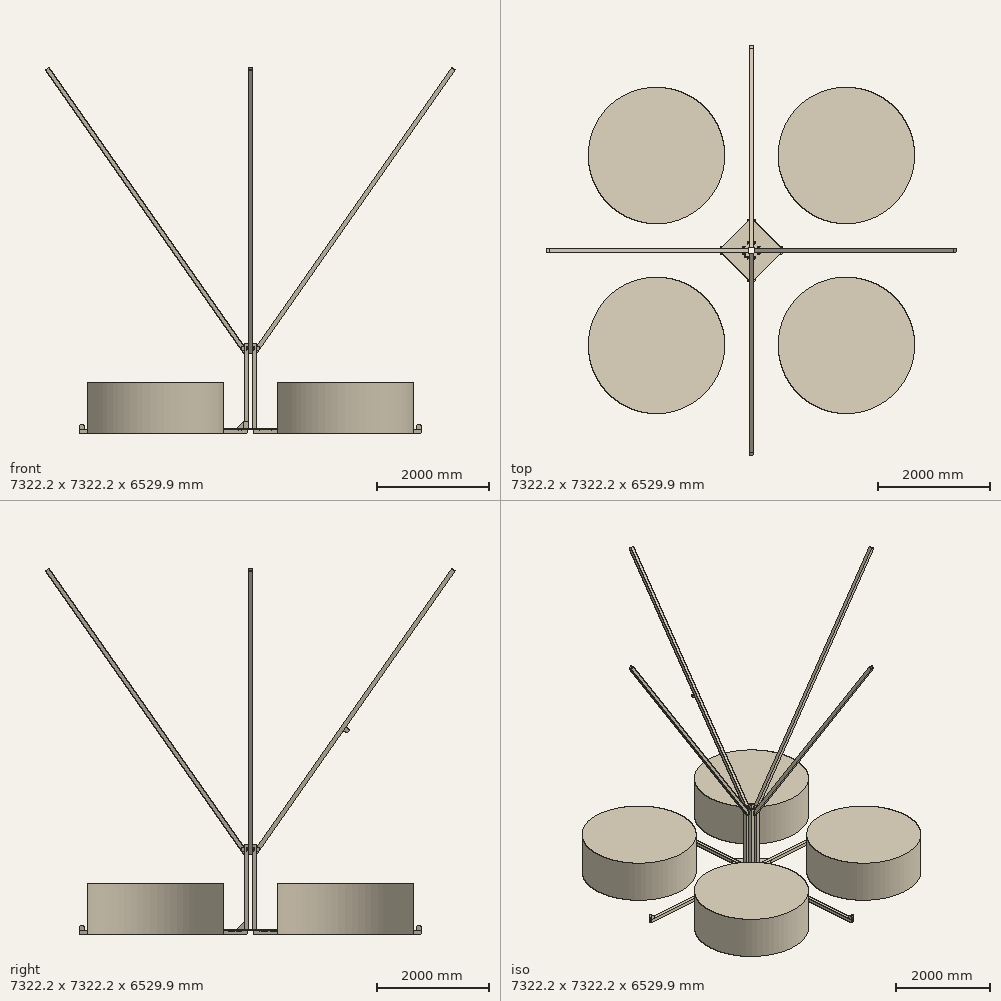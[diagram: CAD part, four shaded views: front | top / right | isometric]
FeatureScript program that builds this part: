
annotation { "Feature Type Name" : "Feature", "Feature Type Description" : "" }
export const myFeature = defineFeature(function(context is Context, id is Id, definition is map)
    precondition{}
    {
        {
            var Q0;
            Q0=qCreatedBy(makeId("Right.planeOp"),FACE);
            cPlane(context, id + "F0", {"entities" : qUnion([Q0]), "cplaneType" : CPlaneType.OFFSET, "offset" : 50.8 * mm, "oppositeDirection" : true, "width" : 152.4 * mm, "height" : 152.4 * mm});
        }
        {
            var Q0;
            Q0=qCreatedBy(id+"F0.planeOp",FACE);
            var sketch = newSketch(context, id + "F1", { "sketchPlane" : qUnion([Q0])});
            skLineSegment(sketch, "E0.bottom", {"start": v(38.1, 38.1) * mm, "end": v(-38.1, 38.1) * mm});
            skLineSegment(sketch, "E0.top", {"start": v(38.1, -38.1) * mm, "end": v(-38.1, -38.1) * mm});
            skLineSegment(sketch, "E0.left", {"start": v(38.1, 38.1) * mm, "end": v(38.1, -38.1) * mm});
            skLineSegment(sketch, "E0.right", {"start": v(-38.1, 38.1) * mm, "end": v(-38.1, -38.1) * mm});
            skPoint(sketch, "E0.middle", {"position": v(0, 0) * mm});
            skLineSegment(sketch, "E1.bottom", {"start": v(35.43, 35.43) * mm, "end": v(-35.43, 35.43) * mm});
            skLineSegment(sketch, "E1.top", {"start": v(35.43, -35.43) * mm, "end": v(-35.43, -35.43) * mm});
            skLineSegment(sketch, "E1.left", {"start": v(35.43, 35.43) * mm, "end": v(35.43, -35.43) * mm});
            skLineSegment(sketch, "E1.right", {"start": v(-35.43, 35.43) * mm, "end": v(-35.43, -35.43) * mm});
            skSolve(sketch);
        }
        {
            var Q0;
            Q0=makeQuery(id+"F1.imprint","IMPRINT",FACE,{"disambiguationData":[TD([[makeQuery(id+"F1.imprint","IMPRINT",EDGE,{"derivedFrom":sQuery(id+"F1.wireOp",EDGE,"E0.bottom")}),1.0]])]});
            extrude(context, id + "F2", {"entities" : qUnion([Q0]), "oppositeDirection" : true, "depth" : 2997.2 * mm});
        }
        {
            var Q0;
            Q0=qCreatedBy(makeId("Right.planeOp"),FACE);
            var sketch = newSketch(context, id + "F3", { "sketchPlane" : qUnion([Q0])});
            skLineSegment(sketch, "E2", {"start": v(0, 0) * mm, "end": v(0, 32.07) * mm, "construction": true});
            skSolve(sketch);
        }
        {
            var Q0;
            Q0=makeQuery(id+"F2.opExtrude","SWEPT_BODY",BODY,{"disambiguationData":[OSD([sQuery(id+"F1.wireOp",EDGE,"E0.bottom"),sQuery(id+"F1.wireOp",EDGE,"E0.top"),sQuery(id+"F1.wireOp",EDGE,"E0.left"),sQuery(id+"F1.wireOp",EDGE,"E0.right"),sQuery(id+"F1.wireOp",EDGE,"E1.bottom"),sQuery(id+"F1.wireOp",EDGE,"E1.top"),sQuery(id+"F1.wireOp",EDGE,"E1.left"),sQuery(id+"F1.wireOp",EDGE,"E1.right")])]});
            var Q1;
            Q1=sQuery(id+"F3.wireOp",EDGE,"E2");
            circularPattern(context, id + "F4", {"entities" : qUnion([Q0]), "axis" : qUnion([Q1]), "angle" : 90 * degree, "instanceCount" : 4});
        }
        {
            var Q0;
            Q0=qCreatedBy(id+"F0.planeOp",FACE);
            cPlane(context, id + "F5", {"entities" : qUnion([Q0]), "cplaneType" : CPlaneType.OFFSET, "offset" : 88.9 * mm, "oppositeDirection" : true, "width" : 152.4 * mm, "height" : 152.4 * mm});
        }
        {
            var Q0;
            Q0=qCreatedBy(id+"F5.planeOp",FACE);
            var sketch = newSketch(context, id + "F6", { "sketchPlane" : qUnion([Q0])});
            skLineSegment(sketch, "E3", {"start": v(-38.1, 38.1) * mm, "end": v(-63.5, 38.1) * mm});
            skLineSegment(sketch, "E4", {"start": v(-63.5, 38.1) * mm, "end": v(-63.5, 34.93) * mm});
            skLineSegment(sketch, "E5", {"start": v(-63.5, 34.93) * mm, "end": v(-28.58, 34.93) * mm});
            skLineSegment(sketch, "E6", {"start": v(-28.58, 34.93) * mm, "end": v(-28.57, 12.7) * mm});
            skLineSegment(sketch, "E7", {"start": v(-38.1, 12.7) * mm, "end": v(-28.57, 12.7) * mm});
            skLineSegment(sketch, "E8", {"start": v(-38.1, 12.7) * mm, "end": v(-38.1, 38.1) * mm});
            skSolve(sketch);
        }
        {
            var Q0;
            Q0 = qSketchRegion(id + "F6", true);
            extrude(context, id + "F7", {"entities" : qUnion([Q0]), "oppositeDirection" : true, "depth" : 406.4 * mm});
        }
        {
            var Q0;
            Q0=makeQuery(id+"F7.opExtrude","SWEPT_BODY",BODY,{"disambiguationData":[OSD([sQuery(id+"F6.wireOp",EDGE,"E3"),sQuery(id+"F6.wireOp",EDGE,"E4"),sQuery(id+"F6.wireOp",EDGE,"E5"),sQuery(id+"F6.wireOp",EDGE,"E6"),sQuery(id+"F6.wireOp",EDGE,"E7"),sQuery(id+"F6.wireOp",EDGE,"E8")])]});
            var Q1;
            Q1=qCreatedBy(makeId("Front.planeOp"),FACE);
            mirror(context, id + "F8", {"entities" : qUnion([Q0]), "mirrorPlane" : qUnion([Q1])});
        }
        {
            var Q0;
            Q0=makeQuery(id+"F7.opExtrude","SWEPT_BODY",BODY,{"disambiguationData":[OSD([sQuery(id+"F6.wireOp",EDGE,"E3"),sQuery(id+"F6.wireOp",EDGE,"E4"),sQuery(id+"F6.wireOp",EDGE,"E5"),sQuery(id+"F6.wireOp",EDGE,"E6"),sQuery(id+"F6.wireOp",EDGE,"E7"),sQuery(id+"F6.wireOp",EDGE,"E8")])]});
            var Q1;
            Q1=makeQuery(id+"F8.opPattern","COPY",BODY,{"derivedFrom":makeQuery(id+"F7.opExtrude","SWEPT_BODY",BODY,{"disambiguationData":[OSD([sQuery(id+"F6.wireOp",EDGE,"E3"),sQuery(id+"F6.wireOp",EDGE,"E4"),sQuery(id+"F6.wireOp",EDGE,"E5"),sQuery(id+"F6.wireOp",EDGE,"E6"),sQuery(id+"F6.wireOp",EDGE,"E7"),sQuery(id+"F6.wireOp",EDGE,"E8")])]}),"instanceName":"1"});
            var Q2;
            Q2=sQuery(id+"F3.wireOp",EDGE,"E2");
            circularPattern(context, id + "F9", {"entities" : qUnion([Q0, Q1]), "axis" : qUnion([Q2]), "angle" : 90 * degree, "instanceCount" : 4});
        }
        {
            var Q0;
            Q0=qCreatedBy(makeId("Right.planeOp"),FACE);
            var sketch = newSketch(context, id + "F10", { "sketchPlane" : qUnion([Q0])});
            skLineSegment(sketch, "E9", {"start": v(0, 0) * mm, "end": v(0, 43.8) * mm});
            skSolve(sketch);
        }
        {
            var Q0;
            Q0=makeQuery(id+"F7.opExtrude","SWEPT_FACE",FACE,{"disambiguationData":[OSD([sQuery(id+"F6.wireOp",EDGE,"E3")])]});
            var sketch = newSketch(context, id + "F11", { "sketchPlane" : qUnion([Q0])});
            skLineSegment(sketch, "E10.0", {"start": v(-546.1, -38.1) * mm, "end": v(-139.7, -38.1) * mm, "construction": true});
            skLineSegment(sketch, "E10.1", {"start": v(-38.1, -3048) * mm, "end": v(-38.1, -50.8) * mm, "construction": true});
            skLineSegment(sketch, "E10.3", {"start": v(-38.1, -546.1) * mm, "end": v(-63.5, -546.1) * mm, "construction": true});
            skLineSegment(sketch, "E11", {"start": v(-546.1, -38.1) * mm, "end": v(-38.1, -546.1) * mm});
            skLineSegment(sketch, "E12", {"start": v(-38.1, -63.5) * mm, "end": v(-63.5, -38.1) * mm});
            skLineSegment(sketch, "E13", {"start": v(-63.5, -38.1) * mm, "end": v(-546.1, -38.1) * mm});
            skLineSegment(sketch, "E14", {"start": v(-546.1, -38.1) * mm, "end": v(-63.5, -38.1) * mm});
            skLineSegment(sketch, "E15", {"start": v(-38.1, -546.1) * mm, "end": v(-38.1, -63.5) * mm});
            skLineSegment(sketch, "E16", {"start": v(-50.8, -50.8) * mm, "end": v(-292.1, -292.1) * mm, "construction": true});
            skLineSegment(sketch, "E17", {"start": v(-171.45, -171.45) * mm, "end": v(-225.33, -225.33) * mm});
            skLineSegment(sketch, "E18", {"start": v(-225.33, -225.33) * mm, "end": v(-494.74, 44.08) * mm, "construction": true});
            skLineSegment(sketch, "E19", {"start": v(-494.74, 44.08) * mm, "end": v(-386.98, 151.84) * mm, "construction": true});
            skLineSegment(sketch, "E20", {"start": v(-386.98, 151.84) * mm, "end": v(-117.57, -117.57) * mm, "construction": true});
            skLineSegment(sketch, "E21", {"start": v(-117.57, -117.57) * mm, "end": v(-171.45, -171.45) * mm});
            skSolve(sketch);
        }
        {
            var Q0;
            Q0 = qSketchRegion(id + "F11", true);
            extrude(context, id + "F12", {"entities" : qUnion([Q0]), "depth" : 3.17 * mm});
        }
        {
            var Q0;
            Q0=makeQuery(id+"F12.opExtrude","SWEPT_BODY",BODY,{"disambiguationData":[OSD([sQuery(id+"F11.wireOp",EDGE,"E11"),sQuery(id+"F11.wireOp",EDGE,"E12"),sQuery(id+"F11.wireOp",EDGE,"E14"),sQuery(id+"F11.wireOp",EDGE,"E15")])]});
            var Q1;
            Q1=sQuery(id+"F10.wireOp",EDGE,"E9");
            circularPattern(context, id + "F13", {"entities" : qUnion([Q0]), "axis" : qUnion([Q1]), "angle" : 90 * degree, "instanceCount" : 4});
        }
        {
            var Q0;
            Q0=makeQuery(id+"F2.opExtrude","SWEPT_FACE",FACE,{"disambiguationData":[OSD([sQuery(id+"F1.wireOp",EDGE,"E0.bottom")])]});
            var sketch = newSketch(context, id + "F14", { "sketchPlane" : qUnion([Q0])});
            skLineSegment(sketch, "E22.bottom", {"start": v(-3048, 38.1) * mm, "end": v(-2971.8, 38.1) * mm});
            skLineSegment(sketch, "E22.top", {"start": v(-3048, -38.1) * mm, "end": v(-2971.8, -38.1) * mm});
            skLineSegment(sketch, "E22.left", {"start": v(-3048, 38.1) * mm, "end": v(-3048, -38.1) * mm});
            skLineSegment(sketch, "E22.right", {"start": v(-2971.8, 38.1) * mm, "end": v(-2971.8, -38.1) * mm});
            skSolve(sketch);
        }
        {
            var Q0;
            Q0=makeQuery(id+"F14.imprint","IMPRINT",FACE,{"disambiguationData":[TD([[makeQuery(id+"F14.imprint","IMPRINT",EDGE,{"derivedFrom":sQuery(id+"F14.wireOp",EDGE,"E22.bottom")}),-1.0]])]});
            extrude(context, id + "F15", {"entities" : qUnion([Q0]), "depth" : 6.35 * mm});
        }
        {
            var Q0;
            Q0=makeQuery(id+"F15.opExtrude","SWEPT_FACE",FACE,{"disambiguationData":[OSD([sQuery(id+"F14.wireOp",EDGE,"E22.top")])]});
            var sketch = newSketch(context, id + "F16", { "sketchPlane" : qUnion([Q0])});
            skLineSegment(sketch, "E23.bottom", {"start": v(-2971.8, 44.45) * mm, "end": v(-3048, 44.45) * mm});
            skLineSegment(sketch, "E23.top", {"start": v(-2971.8, 82.55) * mm, "end": v(-3048, 82.55) * mm});
            skLineSegment(sketch, "E23.left", {"start": v(-2971.8, 44.45) * mm, "end": v(-2971.8, 82.55) * mm});
            skLineSegment(sketch, "E23.right", {"start": v(-3048, 44.45) * mm, "end": v(-3048, 82.55) * mm});
            skArc(sketch, "E24", {"start": v(-2971.8, 82.55) * mm, "mid": v(-3009.9, 120.65) * mm, "end": v(-3048, 82.55) * mm});
            skCircle(sketch, "E25", {"center": v(-3009.9, 82.55) * mm, "radius": 6.35 * mm});
            skSolve(sketch);
        }
        {
            var Q0;
            {var subQ0=sQuery(id+"F16.wireOp",EDGE,"E24");Q0=makeQuery(id+"F16.imprint","IMPRINT",FACE,{"disambiguationData":[TD([[makeQuery(id+"F16.imprint","IMPRINT",EDGE,{"derivedFrom":subQ0}),1.0]])]});}
            var Q1;
            Q1=makeQuery(id+"F16.imprint","IMPRINT",FACE,{"disambiguationData":[TD([[makeQuery(id+"F16.imprint","IMPRINT",EDGE,{"derivedFrom":sQuery(id+"F16.wireOp",EDGE,"E23.bottom")}),1.0]])]});
            extrude(context, id + "F17", {"entities" : qUnion([Q0, Q1]), "oppositeDirection" : true, "depth" : 6.35 * mm});
        }
        {
            var Q0;
            Q0=makeQuery(id+"F17.opExtrude","SWEPT_BODY",BODY,{"disambiguationData":[OSD([sQuery(id+"F16.wireOp",EDGE,"E23.bottom"),sQuery(id+"F16.wireOp",EDGE,"E23.left"),sQuery(id+"F16.wireOp",EDGE,"E23.right"),sQuery(id+"F16.wireOp",EDGE,"E24"),sQuery(id+"F16.wireOp",EDGE,"E25")])]});
            var Q1;
            Q1=qCreatedBy(makeId("Front.planeOp"),FACE);
            mirror(context, id + "F18", {"operationType" : NewBodyOperationType.ADD, "entities" : qUnion([Q0]), "mirrorPlane" : qUnion([Q1])});
        }
        {
            var Q0;
            Q0=makeQuery(id+"F15.opExtrude","SWEPT_BODY",BODY,{"disambiguationData":[OSD([sQuery(id+"F14.wireOp",EDGE,"E22.bottom"),sQuery(id+"F14.wireOp",EDGE,"E22.top"),sQuery(id+"F14.wireOp",EDGE,"E22.left"),sQuery(id+"F14.wireOp",EDGE,"E22.right")])]});
            var Q1;
            Q1=sQuery(id+"F10.wireOp",EDGE,"E9");
            circularPattern(context, id + "F19", {"entities" : qUnion([Q0]), "axis" : qUnion([Q1]), "angle" : 90 * degree, "instanceCount" : 4});
        }
        {
            var Q0;
            Q0=makeQuery(id+"F13.opPattern","COPY",FACE,{"derivedFrom":makeQuery(id+"F12.opExtrude","CAP_FACE",FACE,{"disambiguationData":[OSD([sQuery(id+"F11.wireOp",EDGE,"E11"),sQuery(id+"F11.wireOp",EDGE,"E12"),sQuery(id+"F11.wireOp",EDGE,"E14"),sQuery(id+"F11.wireOp",EDGE,"E15")])],"isStart":false}),"instanceName":"3"});
            var sketch = newSketch(context, id + "F20", { "sketchPlane" : qUnion([Q0])});
            skLineSegment(sketch, "E26.0", {"start": v(-3048, 38.1) * mm, "end": v(-50.8, 38.1) * mm, "construction": true});
            skLineSegment(sketch, "E26.1", {"start": v(-38.1, 3048) * mm, "end": v(-38.1, 50.8) * mm, "construction": true});
            skLineSegment(sketch, "E27", {"start": v(-50.8, 38.1) * mm, "end": v(-38.1, 38.1) * mm});
            skLineSegment(sketch, "E28", {"start": v(-38.1, 38.1) * mm, "end": v(-38.1, 50.8) * mm});
            skLineSegment(sketch, "E29.bottom", {"start": v(-38.1, 38.1) * mm, "end": v(-114.3, 38.1) * mm});
            skLineSegment(sketch, "E29.top", {"start": v(-38.1, 114.3) * mm, "end": v(-114.3, 114.3) * mm});
            skLineSegment(sketch, "E29.left", {"start": v(-38.1, 38.1) * mm, "end": v(-38.1, 114.3) * mm});
            skLineSegment(sketch, "E29.right", {"start": v(-114.3, 38.1) * mm, "end": v(-114.3, 114.3) * mm});
            skLineSegment(sketch, "E30.0", {"start": v(-40.77, 111.63) * mm, "end": v(-111.63, 111.63) * mm});
            skLineSegment(sketch, "E30.1", {"start": v(-40.77, 40.77) * mm, "end": v(-40.77, 111.63) * mm});
            skLineSegment(sketch, "E30.2", {"start": v(-40.77, 40.77) * mm, "end": v(-111.63, 40.77) * mm});
            skLineSegment(sketch, "E30.3", {"start": v(-111.63, 40.77) * mm, "end": v(-111.63, 111.63) * mm});
            skSolve(sketch);
        }
        {
            var Q0;
            {var subQ11=sQuery(id+"F20.wireOp",EDGE,"E30.1");Q0=makeQuery(id+"F20.imprint","IMPRINT",FACE,{"disambiguationData":[TD([[makeQuery(id+"F20.imprint","IMPRINT",EDGE,{"derivedFrom":subQ11}),-1.0]])]});}
            var Q1;
            {var subQ0=sQuery(id+"F20.wireOp",EDGE,"E29.right");var subQ1=sQuery(id+"F20.wireOp",EDGE,"E29.top");var subQ2=makeQuery(id+"F20.imprint","INTERSECT",VERTEX,{"derivedFrom":[subQ1,subQ0]});Q1=makeQuery(id+"F20.imprint","IMPRINT",FACE,{"disambiguationData":[TD([[makeQuery(id+"F20.imprint","IMPRINT",EDGE,{"disambiguationData":[TD([[subQ2,1.0]])],"derivedFrom":subQ1}),1.0]])]});}
            extrude(context, id + "F21", {"entities" : qUnion([Q0, Q1]), "depth" : 1524 * mm});
        }
        {
            var Q0;
            Q0=makeQuery(id+"F21.opExtrude","SWEPT_FACE",FACE,{"disambiguationData":[OSD([sQuery(id+"F20.wireOp",EDGE,"E29.bottom")])]});
            cPlane(context, id + "F22", {"entities" : qUnion([Q0]), "cplaneType" : CPlaneType.OFFSET, "offset" : 12.7 * mm, "oppositeDirection" : true, "width" : 152.4 * mm, "height" : 152.4 * mm});
        }
        {
            var Q0;
            Q0=qCreatedBy(id+"F22.planeOp",FACE);
            var sketch = newSketch(context, id + "F23", { "sketchPlane" : qUnion([Q0])});
            skLineSegment(sketch, "E31.0", {"start": v(-114.3, 1565.28) * mm, "end": v(-114.3, 41.27) * mm, "construction": true});
            skLineSegment(sketch, "E32.0.0", {"start": v(-114.3, 41.28) * mm, "end": v(-38.1, 41.28) * mm});
            skLineSegment(sketch, "E33.bottom", {"start": v(-114.3, 1514.48) * mm, "end": v(-152.4, 1514.48) * mm});
            skLineSegment(sketch, "E33.top", {"start": v(-114.3, 1438.28) * mm, "end": v(-152.4, 1438.28) * mm});
            skLineSegment(sketch, "E33.left", {"start": v(-114.3, 1514.48) * mm, "end": v(-114.3, 1438.28) * mm});
            skLineSegment(sketch, "E33.right", {"start": v(-152.4, 1514.48) * mm, "end": v(-152.4, 1438.28) * mm});
            skSolve(sketch);
        }
        {
            var Q0;
            Q0=makeQuery(id+"F23.imprint","IMPRINT",FACE,{"disambiguationData":[TD([[makeQuery(id+"F23.imprint","IMPRINT",EDGE,{"derivedFrom":sQuery(id+"F23.wireOp",EDGE,"E33.bottom")}),1.0]])]});
            extrude(context, id + "F24", {"entities" : qUnion([Q0]), "oppositeDirection" : true, "depth" : 12.7 * mm});
        }
        {
            var Q0;
            Q0=makeQuery(id+"F24.opExtrude","CAP_FACE",FACE,{"disambiguationData":[OSD([sQuery(id+"F23.wireOp",EDGE,"E33.bottom"),sQuery(id+"F23.wireOp",EDGE,"E33.top"),sQuery(id+"F23.wireOp",EDGE,"E33.left"),sQuery(id+"F23.wireOp",EDGE,"E33.right")])],"isStart":true});
            var sketch = newSketch(context, id + "F25", { "sketchPlane" : qUnion([Q0])});
            skCircle(sketch, "E34", {"center": v(-133.35, 1476.38) * mm, "radius": 6.35 * mm});
            skPoint(sketch, "E34.centerSnap0", {"position": v(-133.35, 1514.48) * mm});
            skSolve(sketch);
        }
        {
            var Q0;
            Q0=makeQuery(id+"F21.opExtrude","SWEPT_BODY",BODY,{"disambiguationData":[OSD([sQuery(id+"F20.wireOp",EDGE,"E29.bottom"),sQuery(id+"F20.wireOp",EDGE,"E29.top"),sQuery(id+"F20.wireOp",EDGE,"E29.left"),sQuery(id+"F20.wireOp",EDGE,"E29.right"),sQuery(id+"F20.wireOp",EDGE,"E30.0"),sQuery(id+"F20.wireOp",EDGE,"E30.1"),sQuery(id+"F20.wireOp",EDGE,"E30.2"),sQuery(id+"F20.wireOp",EDGE,"E30.3")])]});
            var Q1;
            Q1=sQuery(id+"F10.wireOp",EDGE,"E9");
            circularPattern(context, id + "F26", {"entities" : qUnion([Q0]), "axis" : qUnion([Q1]), "angle" : 90 * degree, "instanceCount" : 4});
        }
        {
            var Q0;
            Q0=makeQuery(id+"F25.imprint","IMPRINT",FACE,{"disambiguationData":[TD([[makeQuery(id+"F25.imprint","IMPRINT",EDGE,{"derivedFrom":sQuery(id+"F25.wireOp",EDGE,"E34")}),1.0]])]});
            extrude(context, id + "F27", {"entities" : qUnion([Q0]), "operationType" : NewBodyOperationType.REMOVE, "endBound" : BoundingType.UP_TO_NEXT, "oppositeDirection" : true, "depth" : 25.4 * mm});
        }
        {
            var Q0;
            Q0=makeQuery(id+"F24.opExtrude","SWEPT_BODY",BODY,{"disambiguationData":[OSD([sQuery(id+"F23.wireOp",EDGE,"E33.bottom"),sQuery(id+"F23.wireOp",EDGE,"E33.top"),sQuery(id+"F23.wireOp",EDGE,"E33.left"),sQuery(id+"F23.wireOp",EDGE,"E33.right")])]});
            var Q1;
            Q1=qCreatedBy(makeId("Front.planeOp"),FACE);
            mirror(context, id + "F28", {"entities" : qUnion([Q0]), "mirrorPlane" : qUnion([Q1])});
        }
        {
            var Q0;
            Q0=makeQuery(id+"F24.opExtrude","SWEPT_BODY",BODY,{"disambiguationData":[OSD([sQuery(id+"F23.wireOp",EDGE,"E33.bottom"),sQuery(id+"F23.wireOp",EDGE,"E33.top"),sQuery(id+"F23.wireOp",EDGE,"E33.left"),sQuery(id+"F23.wireOp",EDGE,"E33.right")])]});
            var Q1;
            Q1=makeQuery(id+"F28.opPattern","COPY",BODY,{"derivedFrom":makeQuery(id+"F24.opExtrude","SWEPT_BODY",BODY,{"disambiguationData":[OSD([sQuery(id+"F23.wireOp",EDGE,"E33.bottom"),sQuery(id+"F23.wireOp",EDGE,"E33.top"),sQuery(id+"F23.wireOp",EDGE,"E33.left"),sQuery(id+"F23.wireOp",EDGE,"E33.right")])]}),"instanceName":"1"});
            var Q2;
            Q2=sQuery(id+"F10.wireOp",EDGE,"E9");
            circularPattern(context, id + "F29", {"operationType" : NewBodyOperationType.ADD, "entities" : qUnion([Q0, Q1]), "axis" : qUnion([Q2]), "angle" : 90 * degree, "instanceCount" : 4});
        }
        {
            var Q0;
            Q0=makeQuery(id+"F28.opPattern","COPY",FACE,{"derivedFrom":makeQuery(id+"F24.opExtrude","CAP_FACE",FACE,{"disambiguationData":[OSD([sQuery(id+"F23.wireOp",EDGE,"E33.bottom"),sQuery(id+"F23.wireOp",EDGE,"E33.top"),sQuery(id+"F23.wireOp",EDGE,"E33.left"),sQuery(id+"F23.wireOp",EDGE,"E33.right")])],"isStart":false}),"instanceName":"1"});
            var sketch = newSketch(context, id + "F30", { "sketchPlane" : qUnion([Q0])});
            skLineSegment(sketch, "E35", {"start": v(-133.35, 1476.38) * mm, "end": v(-165.21, 1454.07) * mm});
            skSolve(sketch);
        }
        {
            var Q0;
            Q0=makeQuery(id+"F28.opPattern","COPY",FACE,{"derivedFrom":makeQuery(id+"F24.opExtrude","SWEPT_FACE",FACE,{"disambiguationData":[OSD([sQuery(id+"F23.wireOp",EDGE,"E33.right")])]}),"instanceName":"1"});
            var Q1;
            Q1=sQuery(id+"F30.wireOp",EDGE,"E35");
            cPlane(context, id + "F31", {"entities" : qUnion([Q0, Q1]), "cplaneType" : CPlaneType.LINE_ANGLE, "offset" : 25.4 * mm, "angle" : 0 * degree, "width" : 152.4 * mm, "height" : 152.4 * mm});
        }
        {
            var Q0;
            Q0=qCreatedBy(id+"F31.planeOp",FACE);
            var sketch = newSketch(context, id + "F32", { "sketchPlane" : qUnion([Q0])});
            skLineSegment(sketch, "E36.0", {"start": v(804.18, -38.1) * mm, "end": v(-69.95, -38.1) * mm, "construction": true});
            skLineSegment(sketch, "E37.0", {"start": v(804.18, 38.1) * mm, "end": v(-69.95, 38.1) * mm, "construction": true});
            skLineSegment(sketch, "E38.left", {"start": v(38.1, -38.1) * mm, "end": v(38.1, -44.88) * mm, "construction": true});
            skLineSegment(sketch, "E38.right", {"start": v(-38.1, -38.1) * mm, "end": v(-38.1, -44.88) * mm, "construction": true});
            skPoint(sketch, "E39.0", {"position": v(737.58, 63.5) * mm});
            skPoint(sketch, "E40.0", {"position": v(737.58, -50.8) * mm});
            skLineSegment(sketch, "E41", {"start": v(737.58, -38.1) * mm, "end": v(737.58, 38.1) * mm, "construction": true});
            skLineSegment(sketch, "E42.bottom", {"start": v(699.48, -38.1) * mm, "end": v(775.68, -38.1) * mm});
            skLineSegment(sketch, "E42.top", {"start": v(699.48, 38.1) * mm, "end": v(775.68, 38.1) * mm});
            skLineSegment(sketch, "E42.left", {"start": v(699.48, -38.1) * mm, "end": v(699.48, 38.1) * mm});
            skLineSegment(sketch, "E42.right", {"start": v(775.68, -38.1) * mm, "end": v(775.68, 38.1) * mm});
            skPoint(sketch, "E42.middle", {"position": v(737.58, 0) * mm});
            skLineSegment(sketch, "E43.bottom", {"start": v(705.83, -31.75) * mm, "end": v(769.33, -31.75) * mm});
            skLineSegment(sketch, "E43.top", {"start": v(705.83, 31.75) * mm, "end": v(769.33, 31.75) * mm});
            skLineSegment(sketch, "E43.left", {"start": v(705.83, -31.75) * mm, "end": v(705.83, 31.75) * mm});
            skLineSegment(sketch, "E43.right", {"start": v(769.33, -31.75) * mm, "end": v(769.33, 31.75) * mm});
            skSolve(sketch);
        }
        {
            var Q0;
            Q0=makeQuery(id+"F32.imprint","IMPRINT",FACE,{"disambiguationData":[TD([[makeQuery(id+"F32.imprint","IMPRINT",EDGE,{"derivedFrom":sQuery(id+"F32.wireOp",EDGE,"E42.bottom")}),1.0]])]});
            extrude(context, id + "F33", {"entities" : qUnion([Q0]), "oppositeDirection" : true, "depth" : 6096 * mm, "hasSecondDirection" : true, "secondDirectionOppositeDirection" : false, "secondDirectionDepth" : 76.2 * mm});
        }
        {
            var Q0;
            Q0=makeQuery(id+"F2.opExtrude","SWEPT_FACE",FACE,{"disambiguationData":[OSD([sQuery(id+"F1.wireOp",EDGE,"E0.top")])]});
            var sketch = newSketch(context, id + "F34", { "sketchPlane" : qUnion([Q0])});
            skLineSegment(sketch, "E44.0", {"start": v(-3352.8, 38.1) * mm, "end": v(-50.8, 38.1) * mm, "construction": true});
            skLineSegment(sketch, "E44.1", {"start": v(-38.1, 3352.8) * mm, "end": v(-38.1, 50.8) * mm, "construction": true});
            skLineSegment(sketch, "E45", {"start": v(-3352.8, 38.1) * mm, "end": v(-38.1, 3352.8) * mm, "construction": true});
            skCircle(sketch, "E46", {"center": v(-1695.45, 1695.45) * mm, "radius": 1219.2 * mm});
            skSolve(sketch);
        }
        {
            var Q0;
            Q0=makeQuery(id+"F33.opExtrude","SWEPT_BODY",BODY,{"disambiguationData":[OSD([sQuery(id+"F32.wireOp",EDGE,"E42.bottom"),sQuery(id+"F32.wireOp",EDGE,"E42.top"),sQuery(id+"F32.wireOp",EDGE,"E42.left"),sQuery(id+"F32.wireOp",EDGE,"E42.right"),sQuery(id+"F32.wireOp",EDGE,"E43.bottom"),sQuery(id+"F32.wireOp",EDGE,"E43.top"),sQuery(id+"F32.wireOp",EDGE,"E43.left"),sQuery(id+"F32.wireOp",EDGE,"E43.right")])]});
            var Q1;
            Q1=sQuery(id+"F10.wireOp",EDGE,"E9");
            circularPattern(context, id + "F35", {"entities" : qUnion([Q0]), "axis" : qUnion([Q1]), "angle" : 90 * degree, "instanceCount" : 4});
        }
        {
            var Q0;
            Q0=makeQuery(id+"F19.opPattern","COPY",FACE,{"derivedFrom":makeQuery(id+"F18.boolean.opBoolean","MERGE",FACE,{"derivedFrom":[makeQuery(id+"F15.opExtrude","SWEPT_FACE",FACE,{"disambiguationData":[OSD([sQuery(id+"F14.wireOp",EDGE,"E22.top")])]}),makeQuery(id+"F17.opExtrude","CAP_FACE",FACE,{"disambiguationData":[OSD([sQuery(id+"F16.wireOp",EDGE,"E23.bottom"),sQuery(id+"F16.wireOp",EDGE,"E23.left"),sQuery(id+"F16.wireOp",EDGE,"E23.right"),sQuery(id+"F16.wireOp",EDGE,"E24"),sQuery(id+"F16.wireOp",EDGE,"E25")])],"isStart":true})]}),"instanceName":"3"});
            var sketch = newSketch(context, id + "F36", { "sketchPlane" : qUnion([Q0])});
            skLineSegment(sketch, "E47", {"start": v(-3009.9, 82.55) * mm, "end": v(-1988.55, 2888.7) * mm, "construction": true});
            skLineSegment(sketch, "E48.0", {"start": v(-3661.08, 6448.07) * mm, "end": v(-120.85, 1392.1) * mm, "construction": true});
            skLineSegment(sketch, "E49", {"start": v(-1708.17, 3659.03) * mm, "end": v(-1664.46, 3596.6) * mm});
            skLineSegment(sketch, "E50", {"start": v(-1664.46, 3596.6) * mm, "end": v(-1700.87, 3571.11) * mm});
            skLineSegment(sketch, "E51", {"start": v(-1708.17, 3659.03) * mm, "end": v(-1744.58, 3633.53) * mm});
            skArc(sketch, "E52", {"start": v(-1744.58, 3633.53) * mm, "mid": v(-1753.94, 3580.47) * mm, "end": v(-1700.87, 3571.11) * mm});
            skCircle(sketch, "E53", {"center": v(-1722.73, 3602.32) * mm, "radius": 6.35 * mm});
            skLineSegment(sketch, "E54", {"start": v(-1669.66, 3592.96) * mm, "end": v(-1713.37, 3655.38) * mm});
            skSolve(sketch);
        }
        {
            var Q0;
            {var subQ0=sQuery(id+"F36.wireOp",EDGE,"E49");Q0=makeQuery(id+"F36.imprint","IMPRINT",FACE,{"disambiguationData":[TD([[makeQuery(id+"F36.imprint","IMPRINT",EDGE,{"derivedFrom":subQ0}),-1.0]])]});}
            extrude(context, id + "F37", {"entities" : qUnion([Q0]), "oppositeDirection" : true, "depth" : 76.2 * mm});
        }
        {
            var Q0;
            {var subQ0=sQuery(id+"F36.wireOp",EDGE,"E52");Q0=makeQuery(id+"F36.imprint","IMPRINT",FACE,{"disambiguationData":[TD([[makeQuery(id+"F36.imprint","IMPRINT",EDGE,{"derivedFrom":subQ0}),1.0]])]});}
            extrude(context, id + "F38", {"entities" : qUnion([Q0]), "oppositeDirection" : true, "depth" : 6.35 * mm});
        }
        {
            var Q0;
            Q0=makeQuery(id+"F38.opExtrude","SWEPT_BODY",BODY,{"disambiguationData":[OSD([sQuery(id+"F36.wireOp",EDGE,"E50"),sQuery(id+"F36.wireOp",EDGE,"E51"),sQuery(id+"F36.wireOp",EDGE,"E52"),sQuery(id+"F36.wireOp",EDGE,"E53"),sQuery(id+"F36.wireOp",EDGE,"E54")])]});
            var Q1;
            Q1=qCreatedBy(makeId("Right.planeOp"),FACE);
            mirror(context, id + "F39", {"operationType" : NewBodyOperationType.ADD, "entities" : qUnion([Q0]), "mirrorPlane" : qUnion([Q1])});
        }
        {
            var Q0;
            Q0=makeQuery(id+"F36.imprint","IMPRINT",FACE,{"disambiguationData":[TD([[makeQuery(id+"F36.imprint","IMPRINT",EDGE,{"derivedFrom":sQuery(id+"F36.wireOp",EDGE,"E53")}),1.0]])]});
            var sketch = newSketch(context, id + "F40", { "sketchPlane" : qUnion([Q0])});
            skPoint(sketch, "E55.0", {"position": v(-1722.73, 3602.32) * mm});
            skPoint(sketch, "E56.0", {"position": v(-3009.9, 82.55) * mm});
            skLineSegment(sketch, "E57", {"start": v(-1722.73, 3602.32) * mm, "end": v(-3009.9, 82.55) * mm, "construction": true});
            skLineSegment(sketch, "E58", {"start": v(-3009.9, 82.55) * mm, "end": v(-3097.03, 114.41) * mm, "construction": true});
            skSolve(sketch);
        }
        {
            var Q0;
            Q0=makeQuery(id+"F34.imprint","IMPRINT",FACE,{"disambiguationData":[TD([[makeQuery(id+"F34.imprint","IMPRINT",EDGE,{"derivedFrom":sQuery(id+"F34.wireOp",EDGE,"E46")}),1.0]])]});
            extrude(context, id + "F41", {"entities" : qUnion([Q0]), "oppositeDirection" : true, "depth" : 914.4 * mm});
        }
        {
            var Q0;
            Q0=makeQuery(id+"F41.opExtrude","SWEPT_BODY",BODY,{"disambiguationData":[OSD([sQuery(id+"F34.wireOp",EDGE,"E46")])]});
            var Q1;
            Q1=sQuery(id+"F10.wireOp",EDGE,"E9");
            circularPattern(context, id + "F42", {"entities" : qUnion([Q0]), "axis" : qUnion([Q1]), "angle" : 90 * degree, "instanceCount" : 4});
        }
        {
            var Q0;
            Q0=makeQuery(id+"F12.opExtrude","CAP_FACE",FACE,{"disambiguationData":[OSD([sQuery(id+"F11.wireOp",EDGE,"E11"),sQuery(id+"F11.wireOp",EDGE,"E12"),sQuery(id+"F11.wireOp",EDGE,"E14"),sQuery(id+"F11.wireOp",EDGE,"E15")])],"isStart":false});
            var sketch = newSketch(context, id + "F43", { "sketchPlane" : qUnion([Q0])});
            skLineSegment(sketch, "E59.0", {"start": v(-114.3, -38.1) * mm, "end": v(-114.3, -114.3) * mm});
            skLineSegment(sketch, "E59.1", {"start": v(-38.1, -114.3) * mm, "end": v(-114.3, -114.3) * mm});
            skLineSegment(sketch, "E59.2", {"start": v(-546.1, -38.1) * mm, "end": v(-63.5, -38.1) * mm, "construction": true});
            skLineSegment(sketch, "E59.3", {"start": v(-38.1, -546.1) * mm, "end": v(-38.1, -63.5) * mm, "construction": true});
            skLineSegment(sketch, "E60", {"start": v(-114.3, -38.1) * mm, "end": v(-117.47, -38.1) * mm});
            skLineSegment(sketch, "E61", {"start": v(-117.47, -38.1) * mm, "end": v(-117.47, -117.47) * mm});
            skLineSegment(sketch, "E62", {"start": v(-117.47, -117.47) * mm, "end": v(-38.1, -117.47) * mm});
            skLineSegment(sketch, "E63", {"start": v(-38.1, -117.47) * mm, "end": v(-38.1, -114.3) * mm});
            skSolve(sketch);
        }
        {
            var Q0;
            Q0=makeQuery(id+"F43.imprint","IMPRINT",FACE,{"disambiguationData":[TD([[makeQuery(id+"F43.imprint","IMPRINT",EDGE,{"derivedFrom":sQuery(id+"F43.wireOp",EDGE,"E59.0")}),-1.0]])]});
            extrude(context, id + "F44", {"entities" : qUnion([Q0]), "depth" : 127 * mm});
        }
        {
            var Q0;
            Q0=makeQuery(id+"F26.opPattern","COPY",FACE,{"derivedFrom":makeQuery(id+"F21.opExtrude","SWEPT_FACE",FACE,{"disambiguationData":[OSD([sQuery(id+"F20.wireOp",EDGE,"E29.left")])]}),"instanceName":"1"});
            var sketch = newSketch(context, id + "F45", { "sketchPlane" : qUnion([Q0])});
            skLineSegment(sketch, "E64.0", {"start": v(117.47, 168.28) * mm, "end": v(117.47, 41.28) * mm});
            skLineSegment(sketch, "E65.0", {"start": v(546.1, 41.28) * mm, "end": v(63.5, 41.28) * mm, "construction": true});
            skLineSegment(sketch, "E66", {"start": v(117.47, 41.28) * mm, "end": v(244.47, 41.28) * mm, "construction": true});
            skLineSegment(sketch, "E67", {"start": v(244.47, 41.28) * mm, "end": v(117.47, 168.28) * mm});
            skLineSegment(sketch, "E68", {"start": v(117.47, 41.28) * mm, "end": v(244.47, 41.28) * mm});
            skSolve(sketch);
        }
        {
            var Q0;
            Q0 = qSketchRegion(id + "F45", true);
            extrude(context, id + "F46", {"entities" : qUnion([Q0]), "oppositeDirection" : true, "depth" : 3.17 * mm});
        }
        {
            var Q0;
            Q0=qCreatedBy(makeId("Front.planeOp"),FACE);
            var Q1;
            Q1=qCreatedBy(makeId("Right.planeOp"),FACE);
            cPlane(context, id + "F47", {"entities" : qUnion([Q0, Q1]), "cplaneType" : CPlaneType.MID_PLANE, "offset" : 25.4 * mm, "flipAlignment" : true, "width" : 152.4 * mm, "height" : 152.4 * mm});
        }
        {
            var Q0;
            Q0=makeQuery(id+"F46.opExtrude","SWEPT_BODY",BODY,{"disambiguationData":[OSD([sQuery(id+"F45.wireOp",EDGE,"E64.0"),sQuery(id+"F45.wireOp",EDGE,"E67"),sQuery(id+"F45.wireOp",EDGE,"E68")])]});
            var Q1;
            Q1=qCreatedBy(id+"F47.planeOp",FACE);
            mirror(context, id + "F48", {"operationType" : NewBodyOperationType.ADD, "entities" : qUnion([Q0]), "mirrorPlane" : qUnion([Q1])});
        }
    });
